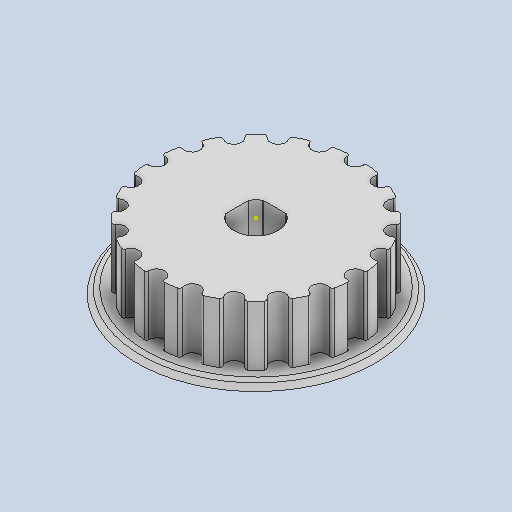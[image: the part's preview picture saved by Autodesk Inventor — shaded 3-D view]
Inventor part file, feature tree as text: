
AUTODESK INVENTOR PART (.ipt)
format: ipt  version: 2024 (Build 280153000, 153)  size: 244,224 bytes
history: native  units: in
note: dims shown in document units (in); Inventor stores cm internally (conversion verified against a paired STEP export)
features: sketch x5, other x3
ambient origin geometry x8: Origin, YZ Plane, XZ Plane, XY Plane, X Axis, Y Axis, Z Axis, Center Point
bodies: Solid1 (feature_tree)
feature tree (8):
  other  "MuftaForRemenSmall.ipt"
  other  "Solid1::MuftaForRemenSmall.ipt"
  other  "TaggingFeature1"
  sketch  "Sketch1"  dims[d0=0.3937in]
  sketch  "Sketch2"
  sketch  "Sketch3"
  sketch  "Sketch4"
  sketch  "Sketch5"
